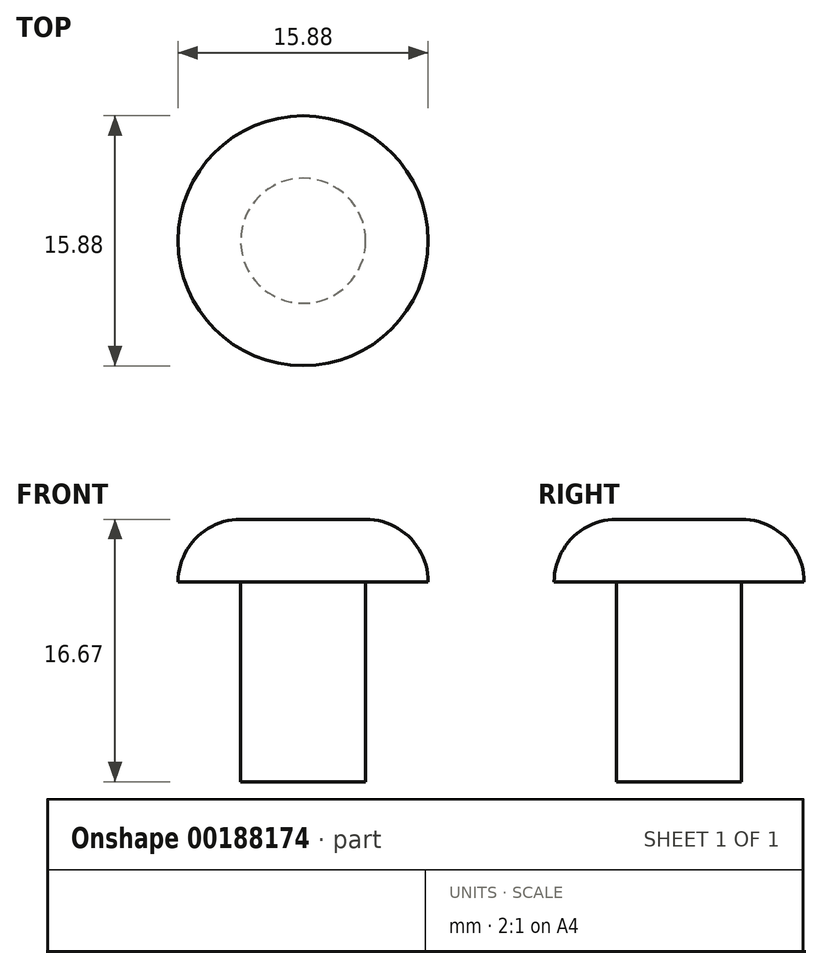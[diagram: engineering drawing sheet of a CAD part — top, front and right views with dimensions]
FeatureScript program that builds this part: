
annotation { "Feature Type Name" : "Feature", "Feature Type Description" : "" }
export const myFeature = defineFeature(function(context is Context, id is Id, definition is map)
    precondition{}
    {
        {
            var Q0;
            Q0=qCreatedBy(makeId("Front.planeOp"),FACE);
            var sketch = newSketch(context, id + "F0", { "sketchPlane" : qUnion([Q0])});
            skLineSegment(sketch, "E0", {"start": v(0, 0) * mm, "end": v(3.97, 0) * mm});
            skLineSegment(sketch, "E1", {"start": v(3.97, 0) * mm, "end": v(3.97, 12.7) * mm});
            skLineSegment(sketch, "E2", {"start": v(3.97, 12.7) * mm, "end": v(7.94, 12.7) * mm});
            skLineSegment(sketch, "E3", {"start": v(0, 0) * mm, "end": v(0, 16.67) * mm});
            skLineSegment(sketch, "E4", {"start": v(0, 16.67) * mm, "end": v(3.97, 16.67) * mm});
            skLineSegment(sketch, "E5", {"start": v(0, 34.26) * mm, "end": v(0, -4.12) * mm, "construction": true});
            skArc(sketch, "E6", {"start": v(7.94, 12.7) * mm, "mid": v(6.78, 15.5) * mm, "end": v(3.97, 16.67) * mm});
            skSolve(sketch);
        }
        {
            var Q0;
            Q0=makeQuery(id+"F0.imprint","IMPRINT",FACE,{"disambiguationData":[TD([[makeQuery(id+"F0.imprint","IMPRINT",EDGE,{"derivedFrom":sQuery(id+"F0.wireOp",EDGE,"E0")}),1.0]])]});
            var Q1;
            Q1=sQuery(id+"F0.wireOp",EDGE,"E5");
            revolve(context, id + "F1", {"entities" : qUnion([Q0]), "axis" : qUnion([Q1]), "revolveType" : RevolveType.FULL});
        }
    });
